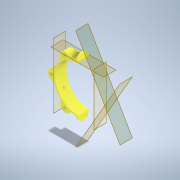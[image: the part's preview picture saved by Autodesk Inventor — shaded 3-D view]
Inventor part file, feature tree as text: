
AUTODESK INVENTOR PART (.ipt)
format: ipt  version: 2021.2 (Build 252289000, 289)  size: 506,880 bytes
history: native  units: in
note: dims shown in document units (in); Inventor stores cm internally (conversion verified against a paired STEP export)
features: extrude x12, sketch x11, plane x5, pattern_circular x4, fillet x2, mirror x1
ambient origin geometry x8: Origin, YZ Plane, XZ Plane, XY Plane, X Axis, Y Axis, Z Axis, Center Point
bodies: Solid1 (feature_tree)
feature tree (35):
  extrude  "Extrusion1"  Depth=4.25in
  plane  "Work Plane1"
  plane  "Work Plane2"
  extrude  "Extrusion3"  Depth=2.125in
  fillet  "Fillet1"  Radius=2.125in
  extrude  "Extrusion4"  TaperAngle=0.0deg  [1 undecoded]
  pattern_circular  "Circular Pattern2"  Count=2 Angle=360.0deg
  plane  "Work Plane3"
  extrude  "Extrusion8"  Depth=1.0in
  extrude  "Extrusion9"  Depth=0.5in
  fillet  "Fillet3"  [1 undecoded]
  extrude  "Extrusion10"  Depth=1.0in
  pattern_circular  "Circular Pattern4"  [2 undecoded]
  extrude  "Extrusion11"  Depth=1.0in
  mirror  "Mirror1"
  plane  "Work Plane4"
  sketch  "Sketch11"  dims[d17=0.2in]
  extrude  "Extrusion13"  Depth=1.0in TaperAngle=0.0deg
  extrude  "Extrusion14"  Depth=0.5in TaperAngle=0.0deg
  pattern_circular  "Circular Pattern5"  [2 undecoded]
  plane  "Work Plane6"
  extrude  "Extrusion15"  Depth=1.0in
  extrude  "Extrusion16"  Depth=0.25in
  pattern_circular  "Circular Pattern6"  [2 undecoded]
  extrude  "Extrusion17"  Depth=1.0in TaperAngle=360.0deg
  sketch  "Sketch1"  dims[d0=4.0in d1=4.25in]
  sketch  "Sketch3"  dims[d2=1.0in d3=0.0in d4=1.5in d10=2.125in]
  sketch  "Sketch4"  dims[d11=0.25in d12=0.0in]
  sketch  "Sketch8"  dims[d13=0.5in d14=0.0in]
  sketch  "Sketch9"  dims[d15=0.5in]
  sketch  "Sketch10"  dims[d16=0.125in]
  sketch  "Sketch12"  dims[d18=0.5in d19=0.0in d20=0.7874in d21=360.0deg]
  sketch  "Sketch13"  dims[d23=-2.125in d24=1.0in]
  sketch  "Sketch14"  dims[d25=0.25in d26=0.5in d27=0.0in]
  sketch  "Sketch15"  dims[d40=0.25in d41=0.125in d42=0.25in d43=0.2in d49=0.1in d50=0.0in d51=0.5in d52=0.0in d53=0.5in d54=0.2in d55=0.25in d56=0.0in d57=0.0in d58=2.3622in d59=360.0deg d61=0.1in d62=0.0in d63=0.5in d64=0.125in d67=0.5in d68=0.5in d69=0.1in d70=0.0in d71=1.0in d72=0.0in d73=0.7874in d74=360.0deg d76=0.5in d77=0.5in d78=0.1in d79=0.0in d80=0.5in d81=0.125in d82=1.0in d83=0.0in d84=0.7874in d85=360.0deg d87=0.0in d88=0.0in]
note: 8 required parameter values undecoded (feature->parameter linkage not recoverable at this tier; creation-order binding heuristic only, values carry confidence <= 0.55)
